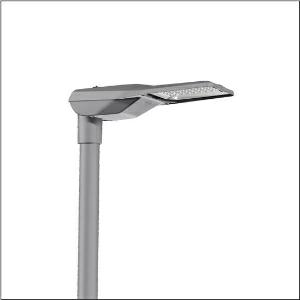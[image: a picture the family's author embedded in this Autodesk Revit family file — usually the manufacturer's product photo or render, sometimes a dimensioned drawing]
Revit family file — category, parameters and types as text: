
# Revit family: streetlight_sl_21_iq_mini___p0_8a_5xe2u31v08hb_1f16
name_source: partatom
category: Lighting Fixtures
units: mm (PartAtom-declared; Revit-internal decimal feet)

## family parameters
Cut with Voids When Loaded = No
Host = Face
Light Source = No
Part Type = Normal
Room Calculation Point = No
Round Connector Dimension = Use Diameter
Shared = No

## types (1)
- --- (1 x LED, 9830 lm, 71 W, 3000K)
    Apparent Load = 71 VA
    CIE Flux Codes = 33 69 96 100 100
    Color Rendering = 70
    Color Temperature = 3000K
    Default Elevation = 1800 mm
    Description = Streetlight SL 21 iQ mini, mast luminaire, primary light control with lens, of PMMA, primary optical cover: cover, of toughened safety glass, transparent, light distribution: P0.8a, light emission: direct distribution, primary light characteristic: asymmetric, installation type: post-top, side-entry, LED, High Power LED, rated luminous flux: 9.830lm, luminous efficacy: 139lm/W, light colour: 730, colour temperature: 3000K, control gear: iQ-Street Remote, D4i with power reduction, control: pre-setting: logarithmic dimming characteristic, Street-Remote, Auto-Match, Temp-Guard, Lumen-Switch, Night-Set, Smart-Wire, Light-Fading, Desk-Remote (wireless, voltage-free reading and setting of iQ features in the workshop via application-optimized NFC function/RFID function), optimised constant luminous flux control (CLO 2.0), mains connection: 220..240V, AC, 50/60Hz, start of lifetime: 71W, end of service life: 75W, reduction: 30W, luminaire housing, of diecast aluminium, powder-coated, SITECO metallic grey (DB 702S), corrosivity category C5 high according to DIN EN ISO 12944, please order mast flange separately, inclination adjustable: 0°, 5°, 10°, 15°, sealing non-destructively replaceable, multi-level sealing system, length: 628mm, width: 235mm, height: 110mm, mast flange for spigot size: 42mm (side-entry): 5XC10008XM4, 60/48mm (side-entry/post-top): 5XC10108XM2, 76/60mm (side-entry/post-top): 5XC10108XM1, mounting height: 4..8m, Smart Interface above, protection rating (complete): IP66, insulation class (complete): insulation class II (safety insulation), certification: CE, ENEC, ENEC+, VDE, impact resistance: IK10, permissible operating ambient temperature for outdoor applications: -40..+50°C, standard-compliant lighting for roads and squares, packaging unit: 1 piece

Light Distribution: P0.8a
    Height = 110 mm
    Lamp = 1 x LED
    Lamp Light Flux = 9830 lm
    Lamp Power = 71 W
    Lamp count = 1
    Length = 625 mm
    Luminous efficacy = 138 lm/W
    Manufacturer = Siteco
    ModVariant = No
    Model = 5XE2U31V08HB
    Mounting Place = Pole
    Mounting Type = Pole top
    Number of Poles = 1
    OnlyDefault = Yes
    Power Factor = 1
    Product Name = Streetlight SL 21 iQ mini | P0.8a
    Product group = mast luminaire | pylon top
    ProductGroupID = 6100
    Protection Class = Protection class II
    Protection Degree = IP 66
    RLX_Detail_Level = 1
    RLX_Emergency_Light_Flux = 0 lm
    RLX_Emergency_Type = 0
    RLX_Emergency_Type_DB = No
    RlxData = <blob elided: 92253 chars, md5=48502668>
    Socket = socket
    Standby Power = 0 W
    System Light Flux = 9830 lm
    System Power = 71 W
    Type Comments = factory setting: luminous flux: 100 % | dim-lin: 254 | 716 mA
    Type Image = l_1003515.jpg
    URL = http://relux.com
    VarID = @adj_083403
    Voltage = 0 V
    Weight = 0.00 kg
    Width = 234 mm

## geometry (parser evidence)
native form markers: Blend x4, Sweep x11
no freeform markers — native parametric forms only
